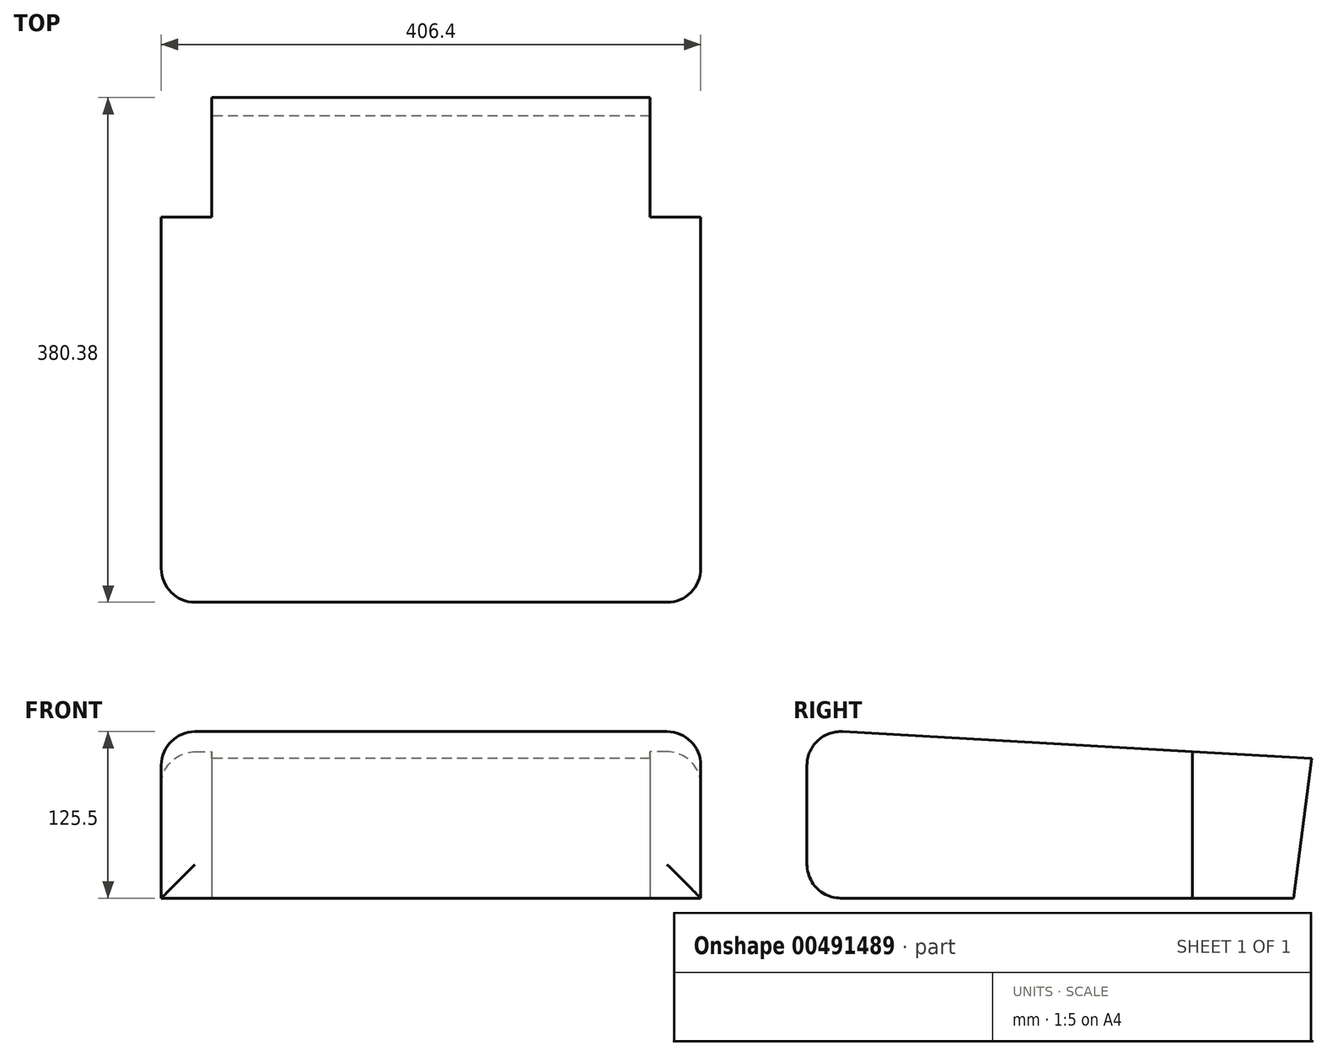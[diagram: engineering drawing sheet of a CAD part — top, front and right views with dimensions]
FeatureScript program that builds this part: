
annotation { "Feature Type Name" : "Feature", "Feature Type Description" : "" }
export const myFeature = defineFeature(function(context is Context, id is Id, definition is map)
    precondition{}
    {
        {
            var Q0;
            Q0=qCreatedBy(makeId("Right.planeOp"),FACE);
            var sketch = newSketch(context, id + "F0", { "sketchPlane" : qUnion([Q0])});
            skLineSegment(sketch, "E0", {"start": v(126.96, 39.05) * mm, "end": v(-253.42, 60.9) * mm});
            skLineSegment(sketch, "E1", {"start": v(-253.42, 60.9) * mm, "end": v(-253.42, -66.1) * mm});
            skLineSegment(sketch, "E2", {"start": v(126.96, 39.05) * mm, "end": v(113.1, -66.1) * mm});
            skLineSegment(sketch, "E3", {"start": v(-253.42, -66.1) * mm, "end": v(113.1, -66.1) * mm});
            skSolve(sketch);
        }
        {
            var Q0;
            Q0=qSketchRegion(id+"F0",true);
            extrude(context, id + "F1", {"entities" : qUnion([Q0]), "depth" : 406.4 * mm});
        }
        {
            var Q0;
            Q0=makeQuery(id+"F1.opExtrude","CAP_EDGE",EDGE,{"disambiguationData":[OSD([sQuery(id+"F0.wireOp",EDGE,"E0")])],"isStart":true});
            var Q1;
            Q1=makeQuery(id+"F1.opExtrude","SWEPT_EDGE",EDGE,{"disambiguationData":[OSD([sQuery(id+"F0.wireOp",EDGE,"E0"),sQuery(id+"F0.wireOp",EDGE,"E1")])]});
            var Q2;
            Q2=makeQuery(id+"F1.opExtrude","CAP_EDGE",EDGE,{"disambiguationData":[OSD([sQuery(id+"F0.wireOp",EDGE,"E0")])],"isStart":false});
            var Q3;
            Q3=makeQuery(id+"F1.opExtrude","CAP_EDGE",EDGE,{"disambiguationData":[OSD([sQuery(id+"F0.wireOp",EDGE,"YyN7SAlZ-oyX6-6t5Q-jrlA-fN3rV7B4wyZS")])],"isStart":true});
            var Q4;
            Q4=makeQuery(id+"F1.opExtrude","CAP_EDGE",EDGE,{"disambiguationData":[OSD([sQuery(id+"F0.wireOp",EDGE,"E1")])],"isStart":true});
            var Q5;
            Q5=makeQuery(id+"F1.opExtrude","SWEPT_EDGE",EDGE,{"disambiguationData":[OSD([sQuery(id+"F0.wireOp",EDGE,"YyN7SAlZ-oyX6-6t5Q-jrlA-fN3rV7B4wyZS"),sQuery(id+"F0.wireOp",EDGE,"E1")])]});
            var Q6;
            Q6=makeQuery(id+"F1.opExtrude","CAP_EDGE",EDGE,{"disambiguationData":[OSD([sQuery(id+"F0.wireOp",EDGE,"E1")])],"isStart":false});
            var Q7;
            Q7=makeQuery(id+"F1.opExtrude","CAP_EDGE",EDGE,{"disambiguationData":[OSD([sQuery(id+"F0.wireOp",EDGE,"YyN7SAlZ-oyX6-6t5Q-jrlA-fN3rV7B4wyZS")])],"isStart":false});
            fillet(context, id + "F2", {"entities" : qUnion([Q0, Q1, Q2, Q3, Q4, Q5, Q6, Q7]), "radius" : 25.4 * mm, "tangentPropagation" : true, "allowEdgeOverflow" : false});
        }
        {
            var Q0;
            Q0=makeQuery(id+"F1.opExtrude","SWEPT_FACE",FACE,{"disambiguationData":[OSD([sQuery(id+"F0.wireOp",EDGE,"E3")])]});
            var sketch = newSketch(context, id + "F3", { "sketchPlane" : qUnion([Q0])});
            skLineSegment(sketch, "E4.bottom", {"start": v(-51.12, -191.01) * mm, "end": v(38.1, -191.01) * mm});
            skLineSegment(sketch, "E4.top", {"start": v(-51.12, -36.9) * mm, "end": v(38.1, -36.9) * mm});
            skLineSegment(sketch, "E4.left", {"start": v(-51.12, -191.01) * mm, "end": v(-51.12, -36.9) * mm});
            skLineSegment(sketch, "E4.right", {"start": v(38.1, -191.01) * mm, "end": v(38.1, -36.9) * mm});
            skLineSegment(sketch, "E5", {"start": v(203.2, -113.1) * mm, "end": v(203.2, 159.34) * mm});
            skLineSegment(sketch, "E6.MirrorCS", {"start": v(368.3, -191.01) * mm, "end": v(368.3, -36.9) * mm});
            skLineSegment(sketch, "E7.MirrorCS", {"start": v(457.52, -36.9) * mm, "end": v(368.3, -36.9) * mm});
            skLineSegment(sketch, "E8.MirrorCS", {"start": v(457.52, -191.01) * mm, "end": v(457.52, -36.9) * mm});
            skLineSegment(sketch, "E9.MirrorCS", {"start": v(457.52, -191.01) * mm, "end": v(368.3, -191.01) * mm});
            skSolve(sketch);
        }
        {
            var Q0;
            Q0=qSketchRegion(id+"F3",true);
            extrude(context, id + "F4", {"entities" : qUnion([Q0]), "operationType" : NewBodyOperationType.REMOVE, "oppositeDirection" : true, "depth" : 127 * mm});
        }
    });
